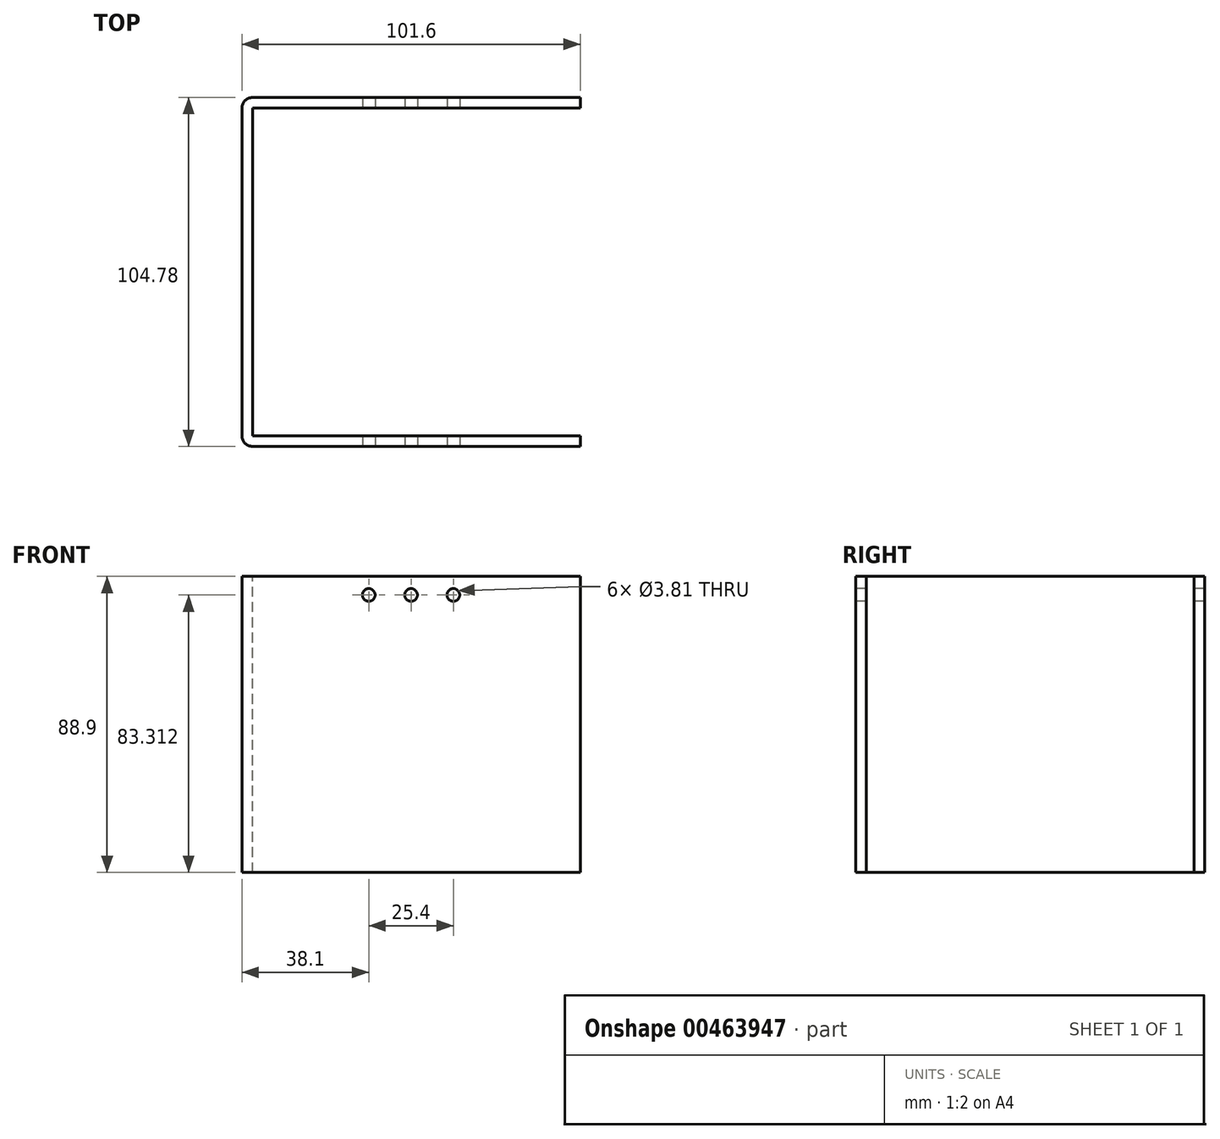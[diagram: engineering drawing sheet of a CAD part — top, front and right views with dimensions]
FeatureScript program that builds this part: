
annotation { "Feature Type Name" : "Feature", "Feature Type Description" : "" }
export const myFeature = defineFeature(function(context is Context, id is Id, definition is map)
    precondition{}
    {
        {
            var Q0;
            Q0=qCreatedBy(makeId("Front.planeOp"),FACE);
            var sketch = newSketch(context, id + "F0", { "sketchPlane" : qUnion([Q0])});
            skLineSegment(sketch, "E0.bottom", {"start": v(0, 0) * mm, "end": v(101.6, 0) * mm});
            skLineSegment(sketch, "E0.top", {"start": v(0, 88.9) * mm, "end": v(101.6, 88.9) * mm});
            skLineSegment(sketch, "E0.left", {"start": v(0, 0) * mm, "end": v(0, 88.9) * mm});
            skLineSegment(sketch, "E0.right", {"start": v(101.6, 0) * mm, "end": v(101.6, 88.9) * mm});
            skSolve(sketch);
        }
        {
            var Q0;
            Q0 = qSketchRegion(id + "F0", true);
            extrude(context, id + "F1", {"entities" : qUnion([Q0]), "depth" : 3.17 * mm, "offsetDistance" : 25.4 * mm});
        }
        {
            var Q0;
            Q0=makeQuery(id+"F1.opExtrude","CAP_FACE",FACE,{"disambiguationData":[OSD([sQuery(id+"F0.wireOp",EDGE,"E0.bottom"),sQuery(id+"F0.wireOp",EDGE,"E0.top"),sQuery(id+"F0.wireOp",EDGE,"E0.left"),sQuery(id+"F0.wireOp",EDGE,"E0.right")])],"isStart":false});
            var sketch = newSketch(context, id + "F2", { "sketchPlane" : qUnion([Q0])});
            skLineSegment(sketch, "E1.bottom", {"start": v(0, 0) * mm, "end": v(3.18, 0) * mm});
            skLineSegment(sketch, "E1.top", {"start": v(0, 88.9) * mm, "end": v(3.17, 88.9) * mm});
            skLineSegment(sketch, "E1.left", {"start": v(0, 0) * mm, "end": v(0, 88.9) * mm});
            skLineSegment(sketch, "E1.right", {"start": v(3.18, 0) * mm, "end": v(3.17, 88.9) * mm});
            skSolve(sketch);
        }
        {
            var Q0;
            Q0 = qSketchRegion(id + "F2", true);
            extrude(context, id + "F3", {"entities" : qUnion([Q0]), "operationType" : NewBodyOperationType.ADD, "depth" : 101.6 * mm});
        }
        {
            var Q0;
            Q0=makeQuery(id+"F3.opExtrude","SWEPT_FACE",FACE,{"disambiguationData":[OSD([sQuery(id+"F2.wireOp",EDGE,"E1.right")])]});
            var sketch = newSketch(context, id + "F4", { "sketchPlane" : qUnion([Q0])});
            skLineSegment(sketch, "E2.bottom", {"start": v(-104.78, 88.9) * mm, "end": v(-101.6, 88.9) * mm});
            skLineSegment(sketch, "E2.top", {"start": v(-104.78, 0) * mm, "end": v(-101.6, 0) * mm});
            skLineSegment(sketch, "E2.left", {"start": v(-104.78, 88.9) * mm, "end": v(-104.78, 0) * mm});
            skLineSegment(sketch, "E2.right", {"start": v(-101.6, 88.9) * mm, "end": v(-101.6, 0) * mm});
            skSolve(sketch);
        }
        {
            var Q0;
            Q0 = qSketchRegion(id + "F4", true);
            var Q1;
            Q1=makeQuery(id+"F1.opExtrude","CAP_VERTEX",VERTEX,{"disambiguationData":[OSD([sQuery(id+"F0.wireOp",EDGE,"E0.top"),sQuery(id+"F0.wireOp",EDGE,"E0.right")])],"isStart":false});
            extrude(context, id + "F5", {"entities" : qUnion([Q0]), "operationType" : NewBodyOperationType.ADD, "endBound" : BoundingType.UP_TO_VERTEX, "endBoundEntityVertex" : qUnion([Q1]), "depth" : 97.8 * mm, "offsetDistance" : 25.4 * mm});
        }
        {
            var Q0;
            Q0=makeQuery(id+"F1.opExtrude","CAP_EDGE",EDGE,{"disambiguationData":[OSD([sQuery(id+"F0.wireOp",EDGE,"E0.left")])],"isStart":true});
            var Q1;
            Q1=makeQuery(id+"F3.opExtrude","CAP_EDGE",EDGE,{"disambiguationData":[OSD([sQuery(id+"F2.wireOp",EDGE,"E1.left")])],"isStart":false});
            fillet(context, id + "F6", {"entities" : qUnion([Q0, Q1]), "radius" : 3.17 * mm, "tangentPropagation" : true, "allowEdgeOverflow" : false});
        }
        {
            var Q0;
            Q0=makeQuery(id+"F5.boolean.opBoolean","MERGE",FACE,{"derivedFrom":[makeQuery(id+"F3.opExtrude","CAP_FACE",FACE,{"disambiguationData":[OSD([sQuery(id+"F2.wireOp",EDGE,"E1.bottom"),sQuery(id+"F2.wireOp",EDGE,"E1.top"),sQuery(id+"F2.wireOp",EDGE,"E1.left"),sQuery(id+"F2.wireOp",EDGE,"E1.right")])],"isStart":false}),makeQuery(id+"F5.opExtrude","SWEPT_FACE",FACE,{"disambiguationData":[OSD([sQuery(id+"F4.wireOp",EDGE,"E2.left")])]})]});
            var sketch = newSketch(context, id + "F7", { "sketchPlane" : qUnion([Q0])});
            skLineSegment(sketch, "E3.bottom", {"start": v(31.75, 89.66) * mm, "end": v(69.85, 89.66) * mm});
            skLineSegment(sketch, "E3.top", {"start": v(31.75, 76.96) * mm, "end": v(69.85, 76.96) * mm});
            skLineSegment(sketch, "E3.left", {"start": v(31.75, 89.66) * mm, "end": v(31.75, 76.96) * mm});
            skLineSegment(sketch, "E3.right", {"start": v(69.85, 89.66) * mm, "end": v(69.85, 76.96) * mm});
            skCircle(sketch, "E4", {"center": v(38.1, 83.31) * mm, "radius": 1.9 * mm});
            skCircle(sketch, "E5", {"center": v(50.8, 83.31) * mm, "radius": 1.9 * mm});
            skCircle(sketch, "E6", {"center": v(63.5, 83.31) * mm, "radius": 1.9 * mm});
            skSolve(sketch);
        }
        {
            var Q0;
            Q0=makeQuery(id+"F7.imprint","IMPRINT",FACE,{"disambiguationData":[TD([[makeQuery(id+"F7.imprint","IMPRINT",EDGE,{"derivedFrom":sQuery(id+"F7.wireOp",EDGE,"E4")}),1.0]])]});
            var Q1;
            Q1=makeQuery(id+"F7.imprint","IMPRINT",FACE,{"disambiguationData":[TD([[makeQuery(id+"F7.imprint","IMPRINT",EDGE,{"derivedFrom":sQuery(id+"F7.wireOp",EDGE,"E5")}),1.0]])]});
            var Q2;
            Q2=makeQuery(id+"F7.imprint","IMPRINT",FACE,{"disambiguationData":[TD([[makeQuery(id+"F7.imprint","IMPRINT",EDGE,{"derivedFrom":sQuery(id+"F7.wireOp",EDGE,"E6")}),1.0]])]});
            extrude(context, id + "F8", {"entities" : qUnion([Q0, Q1, Q2]), "operationType" : NewBodyOperationType.REMOVE, "endBound" : BoundingType.THROUGH_ALL, "oppositeDirection" : true, "depth" : 25.4 * mm, "offsetDistance" : 25.4 * mm});
        }
    });
